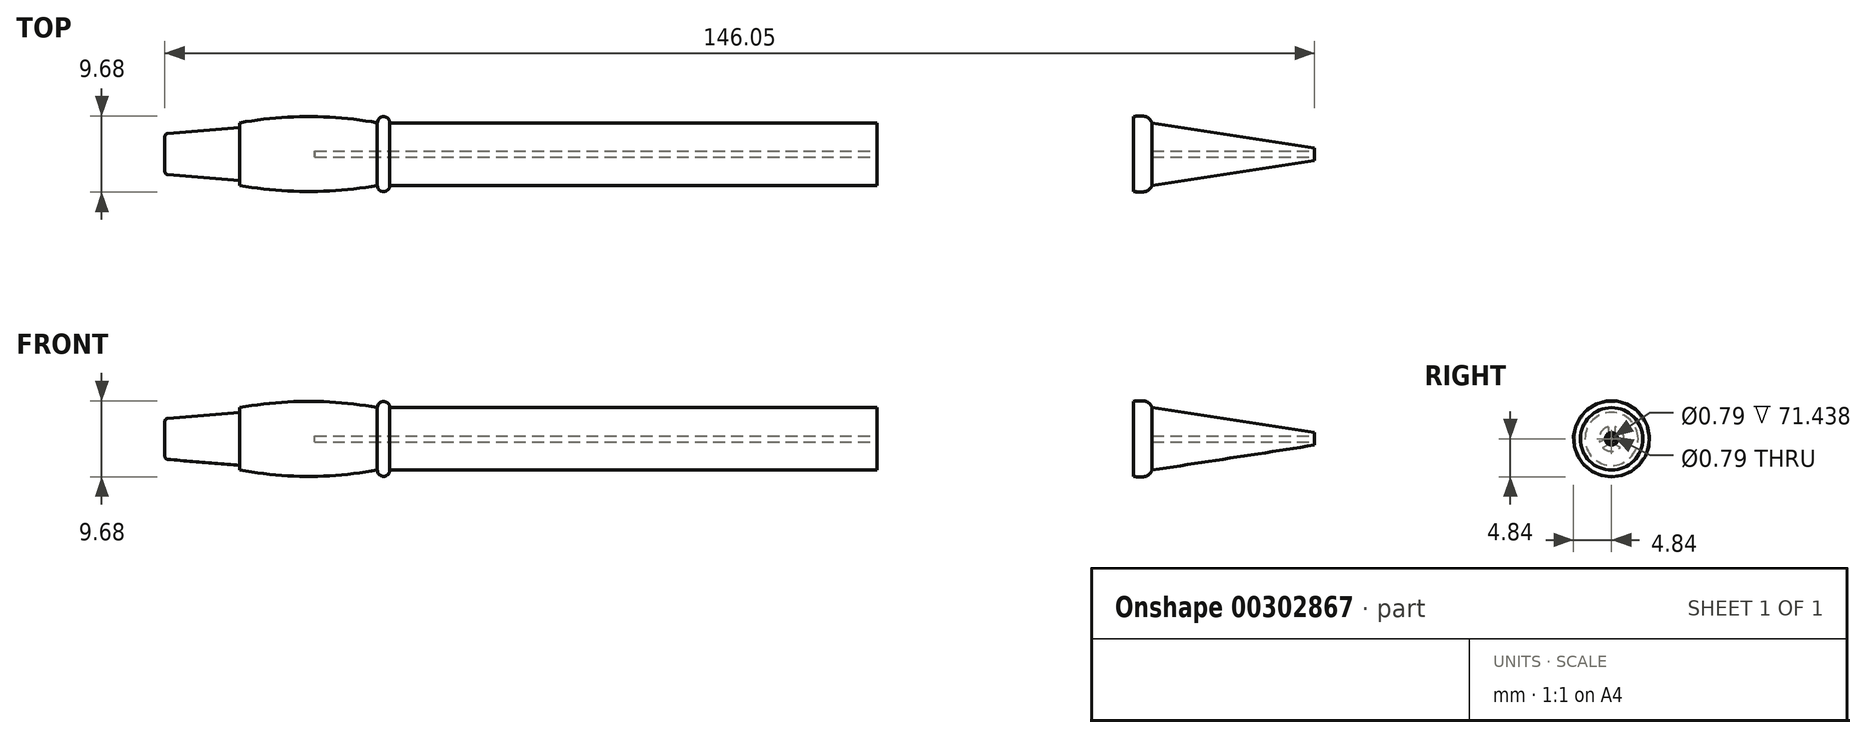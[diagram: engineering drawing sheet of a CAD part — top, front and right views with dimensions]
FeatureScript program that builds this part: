
annotation { "Feature Type Name" : "Feature", "Feature Type Description" : "" }
export const myFeature = defineFeature(function(context is Context, id is Id, definition is map)
    precondition{}
    {
        {
            var Q0;
            Q0=qCreatedBy(makeId("Front.planeOp"),FACE);
            var sketch = newSketch(context, id + "F0", { "sketchPlane" : qUnion([Q0])});
            skLineSegment(sketch, "E0", {"start": v(0, 0) * mm, "end": v(-146.05, 0) * mm});
            skPoint(sketch, "E1", {"position": v(-20.64, 0) * mm});
            skPoint(sketch, "E2", {"position": v(-136.53, 0) * mm});
            skLineSegment(sketch, "E3", {"start": v(0, 0) * mm, "end": v(0, 0.8) * mm});
            skLineSegment(sketch, "E4", {"start": v(-20.64, 0) * mm, "end": v(-20.64, 3.97) * mm});
            skLineSegment(sketch, "E5", {"start": v(-20.64, 3.97) * mm, "end": v(0, 0.8) * mm});
            skPoint(sketch, "E6", {"position": v(-21.43, 4.76) * mm});
            skPoint(sketch, "E7", {"position": v(-46.04, 4.76) * mm});
            skPoint(sketch, "E8", {"position": v(-53.98, 3.97) * mm});
            skPoint(sketch, "E9", {"position": v(-55.56, 3.97) * mm});
            skPoint(sketch, "E10", {"position": v(-54.77, 4.76) * mm});
            skArc(sketch, "E11", {"start": v(-53.98, 3.97) * mm, "mid": v(-54.77, 4.76) * mm, "end": v(-55.56, 3.97) * mm});
            skLineSegment(sketch, "E12", {"start": v(-55.56, 3.97) * mm, "end": v(-55.56, 0) * mm});
            skLineSegment(sketch, "E13", {"start": v(-55.56, 3.97) * mm, "end": v(-117.48, 3.97) * mm});
            skLineSegment(sketch, "E14", {"start": v(-117.48, 3.97) * mm, "end": v(-117.48, 0) * mm});
            skPoint(sketch, "E15", {"position": v(-118.27, 4.76) * mm});
            skPoint(sketch, "E16", {"position": v(-119.06, 3.97) * mm});
            skArc(sketch, "E17", {"start": v(-117.48, 3.97) * mm, "mid": v(-118.27, 4.76) * mm, "end": v(-119.06, 3.97) * mm});
            skLineSegment(sketch, "E18", {"start": v(-136.53, 0) * mm, "end": v(-136.53, 3.97) * mm});
            skPoint(sketch, "E19", {"position": v(-127.8, 4.76) * mm});
            skArc(sketch, "E20", {"start": v(-119.06, 3.97) * mm, "mid": v(-127.8, 4.76) * mm, "end": v(-136.53, 3.97) * mm});
            skLineSegment(sketch, "E21", {"start": v(-146.05, 0) * mm, "end": v(-146.05, 2.21) * mm});
            skPoint(sketch, "E22", {"position": v(-136.53, 3.37) * mm});
            skLineSegment(sketch, "E23", {"start": v(-145.69, 2.61) * mm, "end": v(-136.53, 3.37) * mm});
            skPoint(sketch, "E24.visualSharp", {"position": v(-146.05, 2.58) * mm});
            skArc(sketch, "E24.filletArc", {"start": v(-145.69, 2.61) * mm, "mid": v(-145.95, 2.48) * mm, "end": v(-146.05, 2.21) * mm});
            skFitSpline(sketch, "E25", {"points": [v(-53.98, 3.97) * mm, v(-46.04, 4.76) * mm, v(-28.58, 3.97) * mm, v(-21.43, 4.76) * mm, v(-20.64, 3.97) * mm], "startDerivative": vector(26.27, 4.83) * mm, "endDerivative": vector(5.57, -10) * mm});
            skPoint(sketch, "E26", {"position": v(-21.43, 4.66) * mm});
            skPoint(sketch, "E27", {"position": v(-46.04, 4.66) * mm});
            skPoint(sketch, "E28", {"position": v(-53.98, 3.87) * mm});
            skPoint(sketch, "E29", {"position": v(-20.64, 3.87) * mm});
            skLineSegment(sketch, "E30", {"start": v(-23.02, 4.77) * mm, "end": v(-23.02, 4.67) * mm});
            skLineSegment(sketch, "E31", {"start": v(-23.12, 4.75) * mm, "end": v(-23.12, 4.65) * mm});
            skLineSegment(sketch, "E32", {"start": v(-24.7, 4.5) * mm, "end": v(-24.7, 4.4) * mm});
            skLineSegment(sketch, "E33", {"start": v(-24.8, 4.47) * mm, "end": v(-24.8, 4.38) * mm});
            skLineSegment(sketch, "E34", {"start": v(-26.4, 4.22) * mm, "end": v(-26.4, 4.12) * mm});
            skLineSegment(sketch, "E35", {"start": v(-26.5, 4.2) * mm, "end": v(-26.5, 4.1) * mm});
            skLineSegment(sketch, "E36", {"start": v(-28.08, 4.01) * mm, "end": v(-28.08, 3.91) * mm});
            skLineSegment(sketch, "E37", {"start": v(-28.18, 4) * mm, "end": v(-28.18, 3.9) * mm});
            skLineSegment(sketch, "E38", {"start": v(-29.77, 3.9) * mm, "end": v(-29.77, 3.8) * mm});
            skLineSegment(sketch, "E39", {"start": v(-29.86, 3.9) * mm, "end": v(-29.86, 3.8) * mm});
            skLineSegment(sketch, "E40", {"start": v(-31.45, 3.88) * mm, "end": v(-31.45, 3.78) * mm});
            skLineSegment(sketch, "E41", {"start": v(-31.55, 3.88) * mm, "end": v(-31.55, 3.78) * mm});
            skLineSegment(sketch, "E42", {"start": v(-33.14, 3.92) * mm, "end": v(-33.14, 3.82) * mm});
            skLineSegment(sketch, "E43", {"start": v(-33.24, 3.93) * mm, "end": v(-33.24, 3.83) * mm});
            skLineSegment(sketch, "E44", {"start": v(-34.83, 4) * mm, "end": v(-34.83, 3.9) * mm});
            skLineSegment(sketch, "E45", {"start": v(-34.92, 4.01) * mm, "end": v(-34.92, 3.91) * mm});
            skFitSpline(sketch, "E46.trimOffspring", {"points": [v(-53.98, 3.87) * mm, v(-46.04, 4.66) * mm, v(-28.58, 3.87) * mm, v(-21.43, 4.66) * mm, v(-20.64, 3.87) * mm], "startDerivative": vector(26.27, 4.83) * mm, "endDerivative": vector(5.57, -10) * mm});
            skSolve(sketch);
        }
        {
            var Q0;
            {var subQ1=sQuery(id+"F0.wireOp",EDGE,"E21");Q0=makeQuery(id+"F0.imprint","IMPRINT",FACE,{"disambiguationData":[TD([[makeQuery(id+"F0.imprint","IMPRINT",EDGE,{"derivedFrom":subQ1}),-1.0]])]});}
            var Q1;
            {var subQ0=sQuery(id+"F0.wireOp",EDGE,"E14");Q1=makeQuery(id+"F0.imprint","IMPRINT",FACE,{"disambiguationData":[TD([[makeQuery(id+"F0.imprint","IMPRINT",EDGE,{"derivedFrom":subQ0}),-1.0]])]});}
            var Q2;
            {var subQ0=sQuery(id+"F0.wireOp",EDGE,"E12");Q2=makeQuery(id+"F0.imprint","IMPRINT",FACE,{"disambiguationData":[TD([[makeQuery(id+"F0.imprint","IMPRINT",EDGE,{"derivedFrom":subQ0}),-1.0]])]});}
            var Q3;
            {var subQ1=sQuery(id+"F0.wireOp",EDGE,"E4");Q3=makeQuery(id+"F0.imprint","IMPRINT",FACE,{"disambiguationData":[TD([[makeQuery(id+"F0.imprint","IMPRINT",EDGE,{"derivedFrom":subQ1}),1.0]])]});}
            var Q4;
            {var subQ0=sQuery(id+"F0.wireOp",EDGE,"E3");Q4=makeQuery(id+"F0.imprint","IMPRINT",FACE,{"disambiguationData":[TD([[makeQuery(id+"F0.imprint","IMPRINT",EDGE,{"derivedFrom":subQ0}),1.0]])]});}
            var Q5;
            Q5=sQuery(id+"F0.wireOp",EDGE,"E0");
            revolve(context, id + "F1", {"entities" : qUnion([Q0, Q1, Q2, Q3, Q4]), "axis" : qUnion([Q5]), "revolveType" : RevolveType.FULL});
        }
        {
            var Q0;
            Q0=makeQuery(id+"F1.opRevolve","SWEPT_FACE",FACE,{"disambiguationData":[OSD([sQuery(id+"F0.wireOp",EDGE,"E3")])]});
            var sketch = newSketch(context, id + "F2", { "sketchPlane" : qUnion([Q0])});
            skCircle(sketch, "E47", {"center": v(0, 0) * mm, "radius": 0.4 * mm});
            skSolve(sketch);
        }
        {
            var Q0;
            Q0=makeQuery(id+"F2.imprint","IMPRINT",FACE,{"disambiguationData":[TD([[makeQuery(id+"F2.imprint","IMPRINT",EDGE,{"derivedFrom":sQuery(id+"F2.wireOp",EDGE,"E47")}),1.0]])]});
            extrude(context, id + "F3", {"entities" : qUnion([Q0]), "operationType" : NewBodyOperationType.REMOVE, "oppositeDirection" : true, "depth" : 127 * mm});
        }
        {
            var Q0;
            Q0=makeQuery(id+"F1.opRevolve","SWEPT_FACE",FACE,{"disambiguationData":[OSD([sQuery(id+"F0.wireOp",EDGE,"E21")])]});
            var sketch = newSketch(context, id + "F4", { "sketchPlane" : qUnion([Q0])});
            skCircle(sketch, "E48", {"center": v(0, 0) * mm, "radius": 1.59 * mm});
            skCircle(sketch, "E49", {"center": v(0, 0) * mm, "radius": 0.8 * mm});
            skLineSegment(sketch, "E50", {"start": v(-0.4, 1.54) * mm, "end": v(-0.4, 0.69) * mm});
            skLineSegment(sketch, "E51", {"start": v(0.4, 1.54) * mm, "end": v(0.4, 0.69) * mm});
            skLineSegment(sketch, "E52", {"start": v(-1.53, -0.42) * mm, "end": v(-0.8, 0) * mm});
            skLineSegment(sketch, "E53", {"start": v(-1.13, -1.11) * mm, "end": v(-0.4, -0.69) * mm});
            skLineSegment(sketch, "E54", {"start": v(1.13, -1.11) * mm, "end": v(0.4, -0.69) * mm});
            skLineSegment(sketch, "E55", {"start": v(1.53, -0.42) * mm, "end": v(0.8, 0) * mm});
            skSolve(sketch);
        }
        {
            var Q0;
            {var subQ0=sQuery(id+"F4.wireOp",EDGE,"E50");Q0=makeQuery(id+"F4.imprint","IMPRINT",FACE,{"disambiguationData":[TD([[makeQuery(id+"F4.imprint","IMPRINT",EDGE,{"derivedFrom":subQ0}),-1.0]])]});}
            var Q1;
            {var subQ0=sQuery(id+"F4.wireOp",EDGE,"E51");Q1=makeQuery(id+"F4.imprint","IMPRINT",FACE,{"disambiguationData":[TD([[makeQuery(id+"F4.imprint","IMPRINT",EDGE,{"derivedFrom":subQ0}),1.0]])]});}
            var Q2;
            {var subQ0=sQuery(id+"F4.wireOp",EDGE,"E53");Q2=makeQuery(id+"F4.imprint","IMPRINT",FACE,{"disambiguationData":[TD([[makeQuery(id+"F4.imprint","IMPRINT",EDGE,{"derivedFrom":subQ0}),-1.0]])]});}
            extrude(context, id + "F5", {"entities" : qUnion([Q0, Q1, Q2]), "operationType" : NewBodyOperationType.REMOVE, "oppositeDirection" : true, "depth" : 1 / 101.6 * mm});
        }
    });
